# Revit family: F1100-C-5-1 R1
name_source: partatom
category: Plumbing Fixtures
revit_build: Autodesk Revit 2018 (Build: 20170223_1515(x64)
units: mm (PartAtom-declared; Revit-internal decimal feet)

## family parameters
Always vertical = Yes
Cut with Voids When Loaded = No
Host = Floor
Part Type = Normal
Room Calculation Point = No
Round Connector Dimension = Use Radius
Shared = No

## types (5) — shared parameters
Description = Floor Drain with 5" round strainer
Manufacturer = MIFAB
Model = F1100-C
Rad = 2"

## per-type parameters (varying)
| type | 10" Dia | Other Pipe Sizes | Pipe Diameter | Pipe Rad | Stainer Rad | Strainer Diameter |
| 2" Outlet, 5" Strainer | No | Yes | 2" | 1" | 2 1/2" | 5" |
| 3" Outlet, 6" Strainer | No | Yes | 3" | 1 1/2" | 3" | 6" |
| 4" Outlet, 7" Strainer | No | Yes | 4" | 2" | 3 1/2" | 7" |
| 5" Outlet, 8" Strainer | No | Yes | 5" | 2 1/2" | 4" | 8" |
| 6" Outlet, 10" Strainer | Yes | No | 6" | 3" | 5" | 10" |

## geometry (parser evidence)
native form markers: Sweep x8
no freeform markers — native parametric forms only
